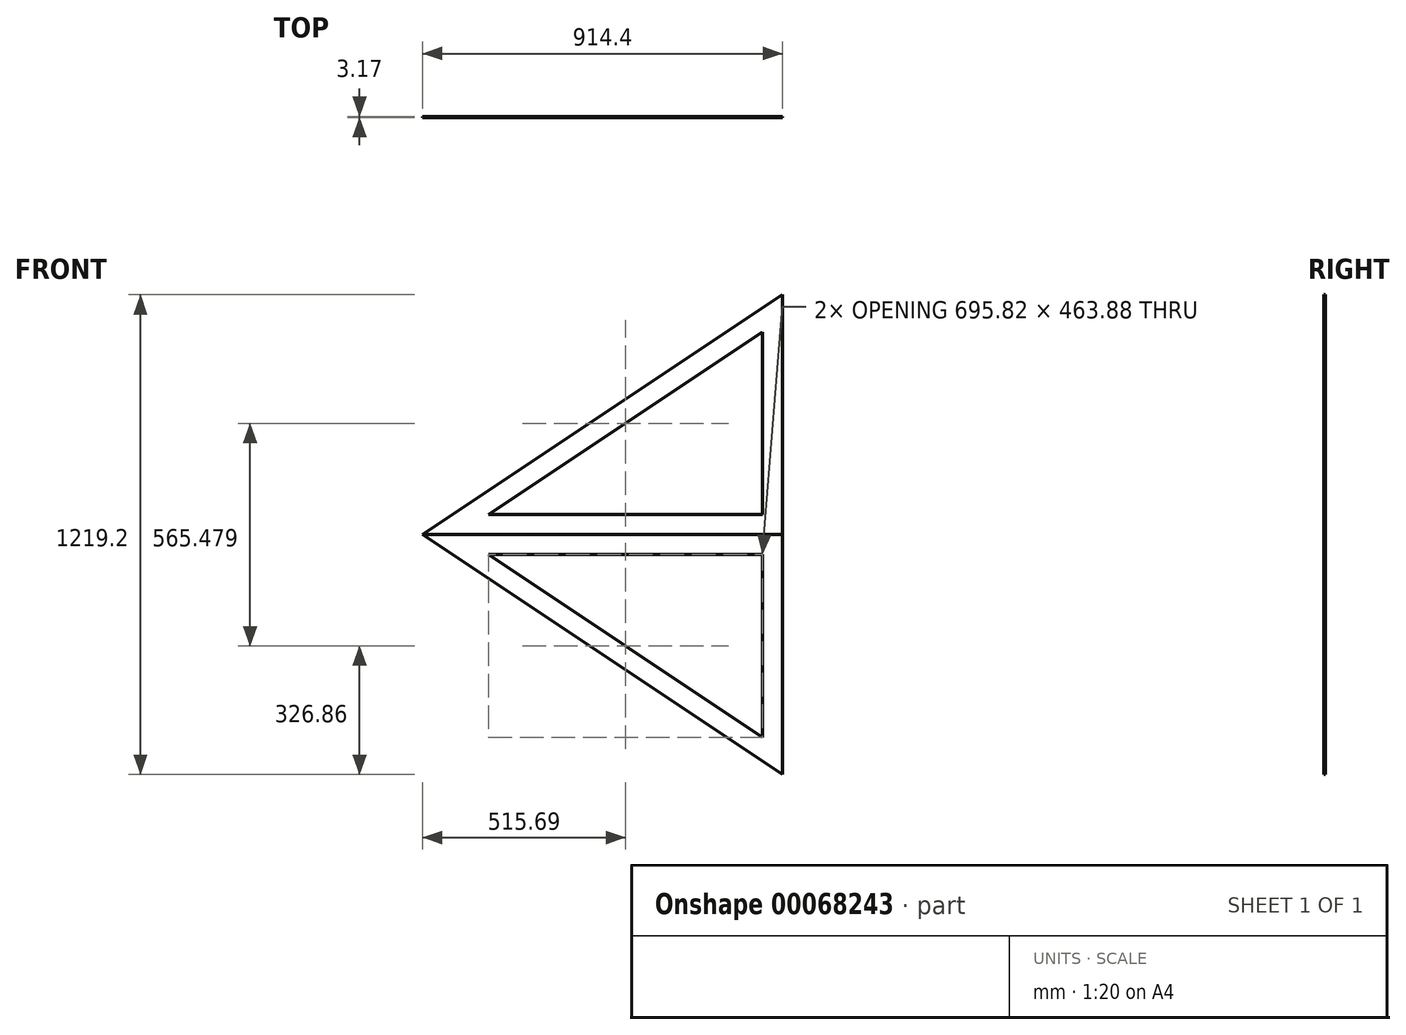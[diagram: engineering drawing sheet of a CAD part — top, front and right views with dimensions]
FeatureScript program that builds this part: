
annotation { "Feature Type Name" : "Feature", "Feature Type Description" : "" }
export const myFeature = defineFeature(function(context is Context, id is Id, definition is map)
    precondition{}
    {
        {
            var Q0;
            Q0=qCreatedBy(makeId("Front.planeOp"),FACE);
            var sketch = newSketch(context, id + "F0", { "sketchPlane" : qUnion([Q0])});
            skLineSegment(sketch, "E0", {"start": v(0, 0) * mm, "end": v(0, 609.6) * mm});
            skLineSegment(sketch, "E1", {"start": v(0, 609.6) * mm, "end": v(-914.4, 0) * mm});
            skLineSegment(sketch, "E2", {"start": v(-914.4, 0) * mm, "end": v(0, 0) * mm});
            skLineSegment(sketch, "E3.0", {"start": v(-50.8, 514.68) * mm, "end": v(-746.62, 50.8) * mm});
            skLineSegment(sketch, "E3.1", {"start": v(-50.8, 50.8) * mm, "end": v(-50.8, 514.68) * mm});
            skLineSegment(sketch, "E3.2", {"start": v(-746.62, 50.8) * mm, "end": v(-50.8, 50.8) * mm});
            skLineSegment(sketch, "E4", {"start": v(-1068.62, 0) * mm, "end": v(465.11, 0) * mm, "construction": true});
            skLineSegment(sketch, "E5.MirrorCS", {"start": v(-50.8, -50.8) * mm, "end": v(-50.8, -514.68) * mm});
            skLineSegment(sketch, "E6.MirrorCS", {"start": v(-50.8, -514.68) * mm, "end": v(-746.62, -50.8) * mm});
            skLineSegment(sketch, "E7.MirrorCS", {"start": v(-746.62, -50.8) * mm, "end": v(-50.8, -50.8) * mm});
            skLineSegment(sketch, "E8.MirrorCS", {"start": v(0, 0) * mm, "end": v(0, -609.6) * mm});
            skLineSegment(sketch, "E9.MirrorCS", {"start": v(0, -609.6) * mm, "end": v(-914.4, 0) * mm});
            skSolve(sketch);
        }
        {
            var Q0;
            Q0=makeQuery(id+"F0.imprint","IMPRINT",FACE,{"disambiguationData":[TD([[makeQuery(id+"F0.imprint","IMPRINT",EDGE,{"derivedFrom":sQuery(id+"F0.wireOp",EDGE,"E0")}),1.0]])]});
            extrude(context, id + "F1", {"entities" : qUnion([Q0]), "depth" : 3.17 * mm});
        }
        {
            var Q0;
            Q0=makeQuery(id+"F0.imprint","IMPRINT",FACE,{"disambiguationData":[TD([[makeQuery(id+"F0.imprint","IMPRINT",EDGE,{"derivedFrom":sQuery(id+"F0.wireOp",EDGE,"E2")}),-1.0]])]});
            extrude(context, id + "F2", {"entities" : qUnion([Q0]), "depth" : 3.17 * mm});
        }
    });
